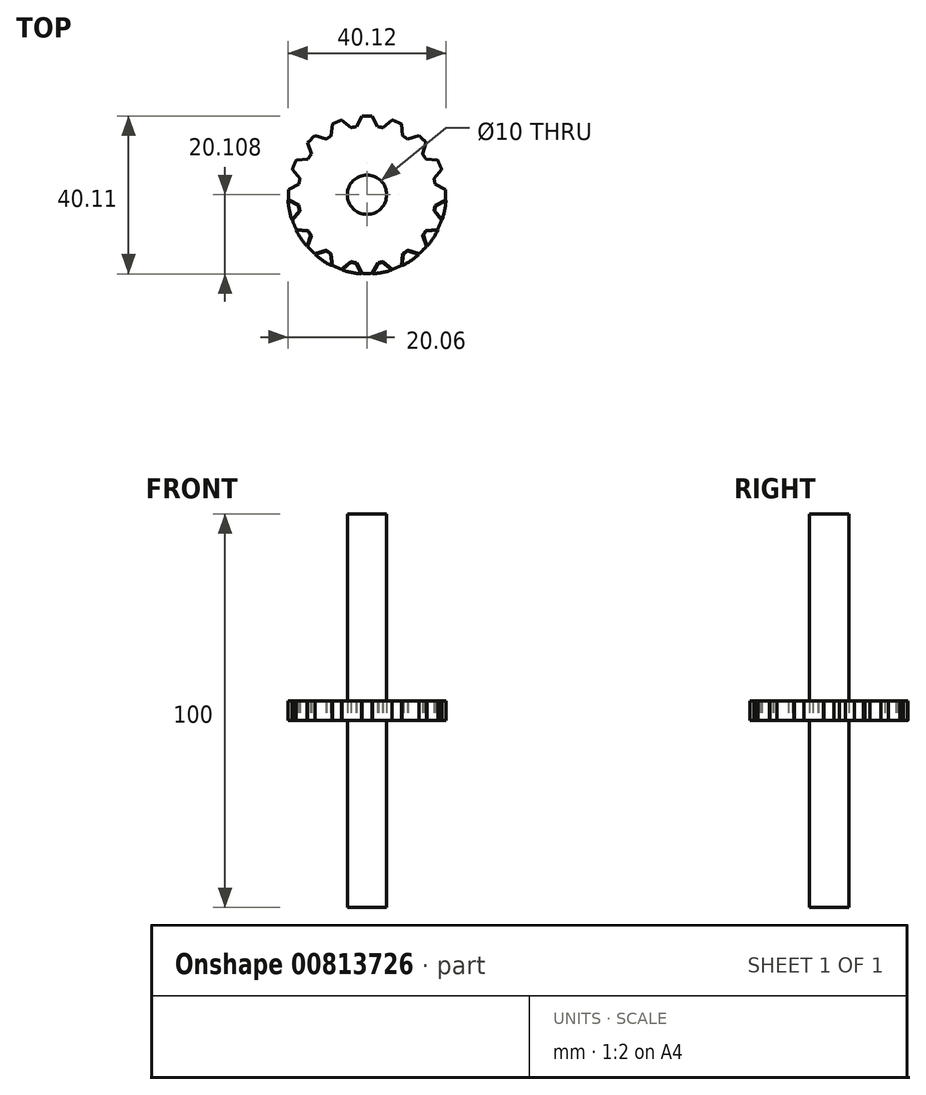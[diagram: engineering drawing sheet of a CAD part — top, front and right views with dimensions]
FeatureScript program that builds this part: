
annotation { "Feature Type Name" : "Feature", "Feature Type Description" : "" }
export const myFeature = defineFeature(function(context is Context, id is Id, definition is map)
    precondition{}
    {
        {
            var Q0;
            Q0=qCreatedBy(makeId("Top.planeOp"),FACE);
            var sketch = newSketch(context, id + "F0", { "sketchPlane" : qUnion([Q0])});
            skArc(sketch, "E0", {"start": v(-6.42, -74.24) * mm, "mid": v(-7.63, -74.7) * mm, "end": v(-8.8, -75.22) * mm});
            skCircle(sketch, "E1", {"center": v(0, -93.18) * mm, "radius": 5 * mm});
            skArc(sketch, "E2", {"start": v(-2.7, -75.9) * mm, "mid": v(-3.4, -76.02) * mm, "end": v(-4.1, -76.17) * mm});
            skLineSegment(sketch, "E3", {"start": v(-14.14, -82.87) * mm, "end": v(-15.04, -80) * mm});
            skLineSegment(sketch, "E4.MirrorCS", {"start": v(-10.3, -79.04) * mm, "end": v(-13.19, -78.15) * mm});
            skLineSegment(sketch, "E5.MirrorCS", {"start": v(-17.3, -90.49) * mm, "end": v(-19.96, -91.9) * mm});
            skLineSegment(sketch, "E6.MirrorCS", {"start": v(-2.7, -75.9) * mm, "end": v(-1.29, -73.22) * mm});
            skLineSegment(sketch, "E7.MirrorCS", {"start": v(-17.3, -95.88) * mm, "end": v(-19.96, -94.47) * mm});
            skLineSegment(sketch, "E8.MirrorCS", {"start": v(2.7, -75.9) * mm, "end": v(1.29, -73.22) * mm});
            skLineSegment(sketch, "E9.MirrorCS", {"start": v(10.3, -79.04) * mm, "end": v(13.19, -78.15) * mm});
            skLineSegment(sketch, "E10.MirrorCS", {"start": v(14.12, -82.85) * mm, "end": v(15, -79.96) * mm});
            skLineSegment(sketch, "E11.MirrorCS", {"start": v(17.3, -90.52) * mm, "end": v(19.96, -91.94) * mm});
            skLineSegment(sketch, "E12.MirrorCS", {"start": v(17.28, -95.94) * mm, "end": v(19.96, -94.5) * mm});
            skLineSegment(sketch, "E13.MirrorCS", {"start": v(14.16, -103.46) * mm, "end": v(15.06, -106.34) * mm});
            skLineSegment(sketch, "E14.MirrorCS", {"start": v(10.36, -107.29) * mm, "end": v(13.25, -108.16) * mm});
            skLineSegment(sketch, "E15.MirrorCS", {"start": v(-14.13, -103.5) * mm, "end": v(-15.04, -106.37) * mm});
            skLineSegment(sketch, "E16.MirrorCS", {"start": v(-10.34, -107.3) * mm, "end": v(-13.22, -108.2) * mm});
            skLineSegment(sketch, "E17.MirrorCS", {"start": v(2.8, -110.45) * mm, "end": v(1.33, -113.14) * mm});
            skLineSegment(sketch, "E18.MirrorCS", {"start": v(-2.67, -110.48) * mm, "end": v(-1.25, -113.14) * mm});
            skLineSegment(sketch, "E19.MirrorCS", {"start": v(14.96, -84.1) * mm, "end": v(17.96, -84.38) * mm});
            skLineSegment(sketch, "E20.MirrorCS", {"start": v(17.01, -89.08) * mm, "end": v(18.94, -86.76) * mm});
            skLineSegment(sketch, "E21.MirrorCS", {"start": v(17.02, -97.26) * mm, "end": v(18.94, -99.6) * mm});
            skLineSegment(sketch, "E22.MirrorCS", {"start": v(14.91, -102.34) * mm, "end": v(17.96, -101.98) * mm});
            skLineSegment(sketch, "E23.MirrorCS", {"start": v(9.08, -108.14) * mm, "end": v(8.8, -111.14) * mm});
            skLineSegment(sketch, "E24.MirrorCS", {"start": v(4.02, -110.21) * mm, "end": v(6.42, -112.12) * mm});
            skLineSegment(sketch, "E25.MirrorCS", {"start": v(-4.1, -110.2) * mm, "end": v(-6.42, -112.12) * mm});
            skLineSegment(sketch, "E26.MirrorCS", {"start": v(-9.1, -108.13) * mm, "end": v(-8.8, -111.14) * mm});
            skLineSegment(sketch, "E27.MirrorCS", {"start": v(-14.97, -102.25) * mm, "end": v(-17.96, -101.98) * mm});
            skLineSegment(sketch, "E28.MirrorCS", {"start": v(-17.01, -97.28) * mm, "end": v(-18.94, -99.6) * mm});
            skLineSegment(sketch, "E29.MirrorCS", {"start": v(-17.01, -89.08) * mm, "end": v(-18.94, -86.76) * mm});
            skLineSegment(sketch, "E30.MirrorCS", {"start": v(-14.96, -84.1) * mm, "end": v(-17.96, -84.38) * mm});
            skLineSegment(sketch, "E31.MirrorCS", {"start": v(-9.08, -78.22) * mm, "end": v(-8.8, -75.22) * mm});
            skLineSegment(sketch, "E32.MirrorCS", {"start": v(-4.1, -76.17) * mm, "end": v(-6.42, -74.24) * mm});
            skLineSegment(sketch, "E33.MirrorCS", {"start": v(4.1, -76.17) * mm, "end": v(6.42, -74.24) * mm});
            skLineSegment(sketch, "E34.MirrorCS", {"start": v(9.08, -78.22) * mm, "end": v(8.8, -75.22) * mm});
            skPoint(sketch, "E35.start.orphan", {"position": v(0, -88.18) * mm});
            skArc(sketch, "E36.trimOffspring", {"start": v(-9.08, -78.22) * mm, "mid": v(-9.7, -78.62) * mm, "end": v(-10.3, -79.04) * mm});
            skArc(sketch, "E37.trimOffspring", {"start": v(-14.14, -82.87) * mm, "mid": v(-14.56, -83.48) * mm, "end": v(-14.96, -84.1) * mm});
            skPoint(sketch, "E38.MirrorCS.end.orphan", {"position": v(-18.48, -85.54) * mm});
            skArc(sketch, "E39.trimOffspring", {"start": v(-17.01, -89.08) * mm, "mid": v(-17.17, -89.78) * mm, "end": v(-17.3, -90.49) * mm});
            skArc(sketch, "E40.trimOffspring", {"start": v(-17.3, -95.88) * mm, "mid": v(-17.17, -96.58) * mm, "end": v(-17.01, -97.28) * mm});
            skArc(sketch, "E41.trimOffspring", {"start": v(-19.96, -91.9) * mm, "mid": v(-20, -93.18) * mm, "end": v(-19.96, -94.47) * mm});
            skArc(sketch, "E42.trimOffspring", {"start": v(-17.96, -84.38) * mm, "mid": v(-18.49, -85.56) * mm, "end": v(-18.94, -86.76) * mm});
            skArc(sketch, "E43.trimOffspring", {"start": v(-13.19, -78.15) * mm, "mid": v(-14.14, -79.04) * mm, "end": v(-15.04, -80) * mm});
            skArc(sketch, "E44.trimOffspring", {"start": v(1.29, -73.22) * mm, "mid": v(0, -73.18) * mm, "end": v(-1.29, -73.22) * mm});
            skPoint(sketch, "E45.MirrorCS.end.orphan", {"position": v(7.64, -74.7) * mm});
            skArc(sketch, "E46.trimOffspring", {"start": v(4.1, -76.17) * mm, "mid": v(3.4, -76.02) * mm, "end": v(2.7, -75.9) * mm});
            skArc(sketch, "E47.trimOffspring", {"start": v(8.8, -75.22) * mm, "mid": v(7.63, -74.7) * mm, "end": v(6.42, -74.24) * mm});
            skArc(sketch, "E48.trimOffspring", {"start": v(10.3, -79.04) * mm, "mid": v(9.7, -78.62) * mm, "end": v(9.08, -78.22) * mm});
            skArc(sketch, "E49.trimOffspring", {"start": v(15, -79.96) * mm, "mid": v(14.13, -79.03) * mm, "end": v(13.19, -78.15) * mm});
            skPoint(sketch, "E50.orphan", {"position": v(18.48, -85.54) * mm});
            skArc(sketch, "E51.trimOffspring", {"start": v(14.96, -84.1) * mm, "mid": v(14.55, -83.46) * mm, "end": v(14.12, -82.85) * mm});
            skArc(sketch, "E52.trimOffspring", {"start": v(17.3, -90.52) * mm, "mid": v(17.17, -89.8) * mm, "end": v(17.01, -89.08) * mm});
            skArc(sketch, "E53.trimOffspring", {"start": v(17.02, -97.26) * mm, "mid": v(17.16, -96.6) * mm, "end": v(17.28, -95.94) * mm});
            skPoint(sketch, "E54.MirrorCS.end.orphan", {"position": v(18.48, -100.83) * mm});
            skArc(sketch, "E55.trimOffspring", {"start": v(14.16, -103.46) * mm, "mid": v(14.55, -102.9) * mm, "end": v(14.91, -102.34) * mm});
            skPoint(sketch, "E56.orphan", {"position": v(7.64, -111.66) * mm});
            skArc(sketch, "E57.trimOffspring", {"start": v(18.94, -86.76) * mm, "mid": v(18.49, -85.56) * mm, "end": v(17.96, -84.38) * mm});
            skArc(sketch, "E58.trimOffspring", {"start": v(19.96, -94.5) * mm, "mid": v(20, -93.22) * mm, "end": v(19.96, -91.94) * mm});
            skArc(sketch, "E59.trimOffspring", {"start": v(17.96, -101.98) * mm, "mid": v(18.49, -100.8) * mm, "end": v(18.94, -99.6) * mm});
            skArc(sketch, "E60.trimOffspring", {"start": v(13.25, -108.16) * mm, "mid": v(14.18, -107.28) * mm, "end": v(15.06, -106.34) * mm});
            skArc(sketch, "E61.trimOffspring", {"start": v(6.42, -112.12) * mm, "mid": v(7.63, -111.67) * mm, "end": v(8.8, -111.14) * mm});
            skArc(sketch, "E62.trimOffspring", {"start": v(-1.25, -113.14) * mm, "mid": v(0.04, -113.18) * mm, "end": v(1.33, -113.14) * mm});
            skArc(sketch, "E63.trimOffspring", {"start": v(-8.8, -111.14) * mm, "mid": v(-7.63, -111.67) * mm, "end": v(-6.42, -112.12) * mm});
            skArc(sketch, "E64.trimOffspring", {"start": v(-18.94, -99.6) * mm, "mid": v(-18.49, -100.8) * mm, "end": v(-17.96, -101.98) * mm});
            skArc(sketch, "E65.trimOffspring", {"start": v(-15.04, -106.37) * mm, "mid": v(-14.16, -107.3) * mm, "end": v(-13.22, -108.2) * mm});
            skArc(sketch, "E66.trimOffspring", {"start": v(-10.34, -107.3) * mm, "mid": v(-9.73, -107.73) * mm, "end": v(-9.1, -108.13) * mm});
            skArc(sketch, "E67.trimOffspring", {"start": v(-14.97, -102.25) * mm, "mid": v(-14.56, -102.89) * mm, "end": v(-14.13, -103.5) * mm});
            skPoint(sketch, "E68.orphan", {"position": v(-7.64, -111.66) * mm});
            skArc(sketch, "E69.trimOffspring", {"start": v(-4.1, -110.2) * mm, "mid": v(-3.4, -110.35) * mm, "end": v(-2.67, -110.48) * mm});
            skArc(sketch, "E70.trimOffspring", {"start": v(2.8, -110.45) * mm, "mid": v(3.42, -110.34) * mm, "end": v(4.02, -110.21) * mm});
            skArc(sketch, "E71.trimOffspring", {"start": v(9.08, -108.14) * mm, "mid": v(9.73, -107.73) * mm, "end": v(10.36, -107.29) * mm});
            skArc(sketch, "E72.2", {"start": v(-17.43, -95.97) * mm, "mid": v(-17.31, -96.61) * mm, "end": v(-17.18, -97.25) * mm});
            skLineSegment(sketch, "E72.3", {"start": v(-17.18, -97.25) * mm, "end": v(-18.88, -99.3) * mm});
            skLineSegment(sketch, "E73.1", {"start": v(-15.06, -102.4) * mm, "end": v(-17.7, -102.15) * mm});
            skArc(sketch, "E73.2", {"start": v(-15.06, -102.4) * mm, "mid": v(-14.69, -102.97) * mm, "end": v(-14.3, -103.53) * mm});
            skLineSegment(sketch, "E73.3", {"start": v(-14.3, -103.53) * mm, "end": v(-15.1, -106.07) * mm});
            skLineSegment(sketch, "E74.0", {"start": v(-10.36, -107.47) * mm, "end": v(-12.92, -108.25) * mm});
            skArc(sketch, "E74.1", {"start": v(-10.36, -107.47) * mm, "mid": v(-9.81, -107.85) * mm, "end": v(-9.25, -108.22) * mm});
            skLineSegment(sketch, "E74.2", {"start": v(-9.25, -108.22) * mm, "end": v(-8.98, -110.89) * mm});
            skLineSegment(sketch, "E75.0", {"start": v(-4.06, -110.36) * mm, "end": v(-6.12, -112.07) * mm});
            skArc(sketch, "E75.1", {"start": v(-4.06, -110.36) * mm, "mid": v(-3.42, -110.5) * mm, "end": v(-2.77, -110.61) * mm});
            skLineSegment(sketch, "E75.2", {"start": v(-2.77, -110.61) * mm, "end": v(-1.5, -112.97) * mm});
            skLineSegment(sketch, "E76.1", {"start": v(2.9, -110.6) * mm, "end": v(1.6, -112.97) * mm});
            skArc(sketch, "E76.2", {"start": v(2.9, -110.6) * mm, "mid": v(3.45, -110.5) * mm, "end": v(3.99, -110.38) * mm});
            skLineSegment(sketch, "E76.3", {"start": v(3.99, -110.38) * mm, "end": v(6.11, -112.07) * mm});
            skLineSegment(sketch, "E77.0", {"start": v(9.23, -108.23) * mm, "end": v(8.97, -110.89) * mm});
            skArc(sketch, "E77.1", {"start": v(9.23, -108.23) * mm, "mid": v(9.81, -107.85) * mm, "end": v(10.38, -107.45) * mm});
            skLineSegment(sketch, "E77.2", {"start": v(10.38, -107.45) * mm, "end": v(12.95, -108.23) * mm});
            skLineSegment(sketch, "E78.0", {"start": v(14.33, -103.49) * mm, "end": v(15.12, -106.04) * mm});
            skArc(sketch, "E78.1", {"start": v(14.33, -103.49) * mm, "mid": v(14.67, -102.99) * mm, "end": v(15, -102.48) * mm});
            skLineSegment(sketch, "E78.2", {"start": v(15, -102.48) * mm, "end": v(17.7, -102.16) * mm});
            skLineSegment(sketch, "E79.1", {"start": v(17.18, -97.22) * mm, "end": v(18.88, -99.3) * mm});
            skArc(sketch, "E79.2", {"start": v(17.18, -97.22) * mm, "mid": v(17.3, -96.63) * mm, "end": v(17.42, -96.03) * mm});
            skLineSegment(sketch, "E79.3", {"start": v(17.42, -96.03) * mm, "end": v(19.79, -94.77) * mm});
            skPoint(sketch, "E80.startSnap0", {"position": v(20, -93.22) * mm});
            skLineSegment(sketch, "E81", {"start": v(-19.96, -91.9) * mm, "end": v(-19.96, -94.47) * mm});
            skLineSegment(sketch, "E82", {"start": v(-19.96, -93.18) * mm, "end": v(-20.1, -93.18) * mm});
            skLineSegment(sketch, "E83", {"start": v(19.96, -91.94) * mm, "end": v(19.96, -94.5) * mm});
            skLineSegment(sketch, "E84", {"start": v(19.96, -93.22) * mm, "end": v(20.1, -93.22) * mm});
            skArc(sketch, "E85.MirrorCS", {"start": v(19.96, 15.8) * mm, "mid": v(20, 14.5) * mm, "end": v(19.96, 13.22) * mm});
            skLineSegment(sketch, "E86.MirrorCS", {"start": v(17.42, 17.32) * mm, "end": v(19.79, 16.06) * mm});
            skArc(sketch, "E87.MirrorCS", {"start": v(-4.1, 31.48) * mm, "mid": v(-3.4, 31.64) * mm, "end": v(-2.67, 31.76) * mm});
            skArc(sketch, "E88.MirrorCS", {"start": v(9.23, 29.52) * mm, "mid": v(9.81, 29.14) * mm, "end": v(10.38, 28.74) * mm});
            skLineSegment(sketch, "E89.MirrorCS", {"start": v(-10.34, 28.59) * mm, "end": v(-13.22, 29.48) * mm});
            skLineSegment(sketch, "E90.MirrorCS", {"start": v(15, 23.77) * mm, "end": v(17.7, 23.45) * mm});
            skArc(sketch, "E91.MirrorCS", {"start": v(18.94, 20.89) * mm, "mid": v(19.61, 18.37) * mm, "end": v(19.96, 15.8) * mm});
            skLineSegment(sketch, "E92.MirrorCS", {"start": v(-9.25, 29.5) * mm, "end": v(-8.98, 32.17) * mm});
            skLineSegment(sketch, "E93.MirrorCS", {"start": v(19.96, 13.22) * mm, "end": v(19.96, 15.8) * mm});
            skLineSegment(sketch, "E94.MirrorCS", {"start": v(10.38, 28.74) * mm, "end": v(12.95, 29.52) * mm});
            skArc(sketch, "E95.MirrorCS", {"start": v(-17.43, 17.26) * mm, "mid": v(-17.31, 17.9) * mm, "end": v(-17.18, 18.53) * mm});
            skLineSegment(sketch, "E96.MirrorCS", {"start": v(17.02, 18.55) * mm, "end": v(18.94, 20.89) * mm});
            skArc(sketch, "E97.MirrorCS", {"start": v(-10.36, 28.76) * mm, "mid": v(-9.81, 29.14) * mm, "end": v(-9.25, 29.5) * mm});
            skLineSegment(sketch, "E98.MirrorCS", {"start": v(-4.06, 31.64) * mm, "end": v(-6.12, 33.35) * mm});
            skLineSegment(sketch, "E99.MirrorCS", {"start": v(-2.67, 31.76) * mm, "end": v(-1.25, 34.43) * mm});
            skArc(sketch, "E100.MirrorCS", {"start": v(2.8, 31.74) * mm, "mid": v(3.42, 31.63) * mm, "end": v(4.02, 31.5) * mm});
            skLineSegment(sketch, "E101.MirrorCS", {"start": v(14.33, 24.77) * mm, "end": v(15.12, 27.32) * mm});
            skLineSegment(sketch, "E102.MirrorCS", {"start": v(4.02, 31.5) * mm, "end": v(6.42, 33.4) * mm});
            skLineSegment(sketch, "E103.MirrorCS", {"start": v(17.28, 17.22) * mm, "end": v(19.96, 15.8) * mm});
            skArc(sketch, "E104.MirrorCS", {"start": v(-19.96, 13.18) * mm, "mid": v(-20, 14.47) * mm, "end": v(-19.96, 15.75) * mm});
            skArc(sketch, "E105.MirrorCS", {"start": v(14.33, 24.77) * mm, "mid": v(14.67, 24.28) * mm, "end": v(15, 23.77) * mm});
            skLineSegment(sketch, "E106.MirrorCS", {"start": v(2.8, 31.74) * mm, "end": v(1.33, 34.42) * mm});
            skLineSegment(sketch, "E107.MirrorCS", {"start": v(19.96, 14.5) * mm, "end": v(20.1, 14.5) * mm});
            skArc(sketch, "E108.MirrorCS", {"start": v(17.18, 18.5) * mm, "mid": v(17.3, 17.92) * mm, "end": v(17.42, 17.32) * mm});
            skArc(sketch, "E109.MirrorCS", {"start": v(15.06, 27.63) * mm, "mid": v(16.65, 25.54) * mm, "end": v(17.96, 23.27) * mm});
            skArc(sketch, "E110.MirrorCS", {"start": v(14.16, 24.75) * mm, "mid": v(14.55, 24.2) * mm, "end": v(14.91, 23.63) * mm});
            skLineSegment(sketch, "E111.MirrorCS", {"start": v(10.36, 28.57) * mm, "end": v(13.25, 29.45) * mm});
            skArc(sketch, "E112.MirrorCS", {"start": v(-10.34, 28.59) * mm, "mid": v(-9.73, 29.01) * mm, "end": v(-9.1, 29.41) * mm});
            skLineSegment(sketch, "E113.MirrorCS", {"start": v(-14.3, 24.82) * mm, "end": v(-15.1, 27.36) * mm});
            skLineSegment(sketch, "E114.MirrorCS", {"start": v(-10.36, 28.76) * mm, "end": v(-12.92, 29.54) * mm});
            skArc(sketch, "E115.MirrorCS", {"start": v(-6.42, 33.4) * mm, "mid": v(-3.87, 34.1) * mm, "end": v(-1.25, 34.43) * mm});
            skArc(sketch, "E116.MirrorCS", {"start": v(17.96, 23.27) * mm, "mid": v(18.49, 22.1) * mm, "end": v(18.94, 20.89) * mm});
            skLineSegment(sketch, "E117.MirrorCS", {"start": v(-14.13, 24.8) * mm, "end": v(-15.04, 27.66) * mm});
            skArc(sketch, "E118.MirrorCS", {"start": v(-4.06, 31.64) * mm, "mid": v(-3.42, 31.78) * mm, "end": v(-2.77, 31.9) * mm});
            skLineSegment(sketch, "E119.MirrorCS", {"start": v(9.23, 29.52) * mm, "end": v(8.97, 32.17) * mm});
            skLineSegment(sketch, "E120.MirrorCS", {"start": v(-19.96, 14.47) * mm, "end": v(-20.1, 14.47) * mm});
            skLineSegment(sketch, "E121.MirrorCS", {"start": v(2.9, 31.88) * mm, "end": v(1.6, 34.25) * mm});
            skLineSegment(sketch, "E122.MirrorCS", {"start": v(-17.43, 17.26) * mm, "end": v(-19.79, 16.01) * mm});
            skArc(sketch, "E123.MirrorCS", {"start": v(-13.22, 29.48) * mm, "mid": v(-11.1, 31.1) * mm, "end": v(-8.8, 32.43) * mm});
            skLineSegment(sketch, "E124.MirrorCS", {"start": v(-2.77, 31.9) * mm, "end": v(-1.5, 34.26) * mm});
            skArc(sketch, "E125.MirrorCS", {"start": v(1.33, 34.42) * mm, "mid": v(3.9, 34.08) * mm, "end": v(6.42, 33.4) * mm});
            skArc(sketch, "E126.MirrorCS", {"start": v(-1.25, 34.43) * mm, "mid": v(0.04, 34.47) * mm, "end": v(1.33, 34.42) * mm});
            skLineSegment(sketch, "E127.MirrorCS", {"start": v(-19.96, 13.18) * mm, "end": v(-19.96, 15.75) * mm});
            skArc(sketch, "E128.MirrorCS", {"start": v(2.9, 31.88) * mm, "mid": v(3.45, 31.78) * mm, "end": v(3.99, 31.66) * mm});
            skArc(sketch, "E129.MirrorCS", {"start": v(-15.04, 27.66) * mm, "mid": v(-14.16, 28.6) * mm, "end": v(-13.22, 29.48) * mm});
            skLineSegment(sketch, "E130.MirrorCS", {"start": v(-15.06, 23.68) * mm, "end": v(-17.7, 23.44) * mm});
            skArc(sketch, "E131.MirrorCS", {"start": v(13.25, 29.45) * mm, "mid": v(14.18, 28.57) * mm, "end": v(15.06, 27.63) * mm});
            skArc(sketch, "E132.MirrorCS", {"start": v(-15.06, 23.68) * mm, "mid": v(-14.69, 24.26) * mm, "end": v(-14.3, 24.82) * mm});
            skArc(sketch, "E133.MirrorCS", {"start": v(8.8, 32.43) * mm, "mid": v(11.12, 31.09) * mm, "end": v(13.25, 29.45) * mm});
            skArc(sketch, "E134.MirrorCS", {"start": v(-19.96, 15.75) * mm, "mid": v(-19.62, 18.36) * mm, "end": v(-18.94, 20.89) * mm});
            skArc(sketch, "E135.MirrorCS", {"start": v(17.02, 18.55) * mm, "mid": v(17.16, 17.89) * mm, "end": v(17.28, 17.22) * mm});
            skArc(sketch, "E136.MirrorCS", {"start": v(9.08, 29.43) * mm, "mid": v(9.73, 29.01) * mm, "end": v(10.36, 28.57) * mm});
            skLineSegment(sketch, "E137.MirrorCS", {"start": v(-4.1, 31.48) * mm, "end": v(-6.42, 33.4) * mm});
            skLineSegment(sketch, "E138.MirrorCS", {"start": v(9.08, 29.43) * mm, "end": v(8.8, 32.43) * mm});
            skLineSegment(sketch, "E139.MirrorCS", {"start": v(-17.18, 18.53) * mm, "end": v(-18.88, 20.59) * mm});
            skLineSegment(sketch, "E140.MirrorCS", {"start": v(3.99, 31.66) * mm, "end": v(6.11, 33.35) * mm});
            skArc(sketch, "E141.MirrorCS", {"start": v(6.42, 33.4) * mm, "mid": v(7.63, 32.96) * mm, "end": v(8.8, 32.43) * mm});
            skLineSegment(sketch, "E142.MirrorCS", {"start": v(17.18, 18.5) * mm, "end": v(18.88, 20.58) * mm});
            skLineSegment(sketch, "E143.MirrorCS", {"start": v(14.91, 23.63) * mm, "end": v(17.96, 23.27) * mm});
            skLineSegment(sketch, "E144.MirrorCS", {"start": v(-17.3, 17.16) * mm, "end": v(-19.96, 15.75) * mm});
            skLineSegment(sketch, "E145.MirrorCS", {"start": v(-9.1, 29.41) * mm, "end": v(-8.8, 32.43) * mm});
            skLineSegment(sketch, "E146.MirrorCS", {"start": v(14.16, 24.75) * mm, "end": v(15.06, 27.63) * mm});
            skArc(sketch, "E147.MirrorCS", {"start": v(-8.8, 32.43) * mm, "mid": v(-7.63, 32.96) * mm, "end": v(-6.42, 33.4) * mm});
            skArc(sketch, "E148.MirrorCS", {"start": v(-17.96, 23.27) * mm, "mid": v(-16.64, 25.56) * mm, "end": v(-15.04, 27.66) * mm});
            skArc(sketch, "E149.MirrorCS", {"start": v(-14.97, 23.53) * mm, "mid": v(-14.56, 24.17) * mm, "end": v(-14.13, 24.8) * mm});
            skLineSegment(sketch, "E150.MirrorCS", {"start": v(-17.01, 18.57) * mm, "end": v(-18.94, 20.89) * mm});
            skArc(sketch, "E151.MirrorCS", {"start": v(-18.94, 20.89) * mm, "mid": v(-18.49, 22.1) * mm, "end": v(-17.96, 23.27) * mm});
            skArc(sketch, "E152.MirrorCS", {"start": v(-17.3, 17.16) * mm, "mid": v(-17.17, 17.87) * mm, "end": v(-17.01, 18.57) * mm});
            skLineSegment(sketch, "E153.MirrorCS", {"start": v(-14.97, 23.53) * mm, "end": v(-17.96, 23.27) * mm});
            skArc(sketch, "E154.MirrorCS", {"start": v(17.3, 11.8) * mm, "mid": v(17.17, 11.08) * mm, "end": v(17.01, 10.37) * mm});
            skLineSegment(sketch, "E155.MirrorCS", {"start": v(-17.3, 11.77) * mm, "end": v(-19.96, 13.18) * mm});
            skLineSegment(sketch, "E156.MirrorCS", {"start": v(17.3, 11.8) * mm, "end": v(19.96, 13.22) * mm});
            skArc(sketch, "E157.MirrorCS", {"start": v(10.3, 0.33) * mm, "mid": v(9.7, -0.1) * mm, "end": v(9.08, -0.49) * mm});
            skLineSegment(sketch, "E158.MirrorCS", {"start": v(17.01, 10.37) * mm, "end": v(18.94, 8.05) * mm});
            skLineSegment(sketch, "E159.MirrorCS", {"start": v(-14.96, 5.38) * mm, "end": v(-17.96, 5.67) * mm});
            skLineSegment(sketch, "E160.MirrorCS", {"start": v(-4.1, -2.54) * mm, "end": v(-6.42, -4.47) * mm});
            skLineSegment(sketch, "E161.MirrorCS", {"start": v(-10.3, 0.33) * mm, "end": v(-13.19, -0.57) * mm});
            skLineSegment(sketch, "E162.MirrorCS", {"start": v(-17.01, 10.37) * mm, "end": v(-18.94, 8.05) * mm});
            skLineSegment(sketch, "E163.MirrorCS", {"start": v(14.96, 5.38) * mm, "end": v(17.96, 5.67) * mm});
            skLineSegment(sketch, "E164.MirrorCS", {"start": v(4.1, -2.54) * mm, "end": v(6.42, -4.47) * mm});
            skLineSegment(sketch, "E165.MirrorCS", {"start": v(9.08, -0.49) * mm, "end": v(8.8, -3.5) * mm});
            skArc(sketch, "E166.MirrorCS", {"start": v(18.94, 8.05) * mm, "mid": v(18.49, 6.84) * mm, "end": v(17.96, 5.67) * mm});
            skLineSegment(sketch, "E167.MirrorCS", {"start": v(2.7, -2.82) * mm, "end": v(1.29, -5.5) * mm});
            skLineSegment(sketch, "E168.MirrorCS", {"start": v(-14.14, 4.16) * mm, "end": v(-15.04, 1.28) * mm});
            skLineSegment(sketch, "E169.MirrorCS", {"start": v(-2.7, -2.82) * mm, "end": v(-1.29, -5.5) * mm});
            skLineSegment(sketch, "E170.MirrorCS", {"start": v(14.12, 4.13) * mm, "end": v(15, 1.25) * mm});
            skArc(sketch, "E171.MirrorCS", {"start": v(-6.42, -4.47) * mm, "mid": v(-7.63, -4.02) * mm, "end": v(-8.8, -3.5) * mm});
            skArc(sketch, "E172.MirrorCS", {"start": v(-17.96, 5.67) * mm, "mid": v(-18.49, 6.84) * mm, "end": v(-18.94, 8.05) * mm});
            skArc(sketch, "E173.MirrorCS", {"start": v(8.8, -3.5) * mm, "mid": v(7.63, -4.02) * mm, "end": v(6.42, -4.47) * mm});
            skArc(sketch, "E174.MirrorCS", {"start": v(-2.7, -2.82) * mm, "mid": v(-3.4, -2.7) * mm, "end": v(-4.1, -2.54) * mm});
            skArc(sketch, "E175.MirrorCS", {"start": v(-9.08, -0.49) * mm, "mid": v(-9.7, -0.1) * mm, "end": v(-10.3, 0.33) * mm});
            skArc(sketch, "E176.MirrorCS", {"start": v(15, 1.25) * mm, "mid": v(14.13, 0.31) * mm, "end": v(13.19, -0.57) * mm});
            skArc(sketch, "E177.MirrorCS", {"start": v(1.29, -5.5) * mm, "mid": v(0, -5.53) * mm, "end": v(-1.29, -5.5) * mm});
            skArc(sketch, "E178.MirrorCS", {"start": v(4.1, -2.54) * mm, "mid": v(3.4, -2.7) * mm, "end": v(2.7, -2.82) * mm});
            skArc(sketch, "E179.MirrorCS", {"start": v(14.96, 5.38) * mm, "mid": v(14.55, 4.75) * mm, "end": v(14.12, 4.13) * mm});
            skArc(sketch, "E180.MirrorCS", {"start": v(-17.01, 10.37) * mm, "mid": v(-17.17, 11.07) * mm, "end": v(-17.3, 11.77) * mm});
            skArc(sketch, "E181.MirrorCS", {"start": v(-14.14, 4.16) * mm, "mid": v(-14.56, 4.76) * mm, "end": v(-14.96, 5.38) * mm});
            skLineSegment(sketch, "E182.MirrorCS", {"start": v(-9.08, -0.49) * mm, "end": v(-8.8, -3.5) * mm});
            skArc(sketch, "E183.MirrorCS", {"start": v(-13.19, -0.57) * mm, "mid": v(-14.14, 0.33) * mm, "end": v(-15.04, 1.28) * mm});
            skLineSegment(sketch, "E184.MirrorCS", {"start": v(10.3, 0.33) * mm, "end": v(13.19, -0.57) * mm});
            skPoint(sketch, "E185.MirrorP", {"position": v(-7.64, 32.95) * mm});
            skPoint(sketch, "E186.MirrorP", {"position": v(18.48, 22.11) * mm});
            skPoint(sketch, "E187.MirrorP", {"position": v(7.64, 32.95) * mm});
            skPoint(sketch, "E188.MirrorP", {"position": v(0, 9.47) * mm});
            skPoint(sketch, "E189.MirrorP", {"position": v(18.48, 6.82) * mm});
            skPoint(sketch, "E190.MirrorP", {"position": v(20, 14.5) * mm});
            skPoint(sketch, "E191.MirrorP", {"position": v(-18.48, 6.82) * mm});
            skCircle(sketch, "E192.MirrorC", {"center": v(0, 14.47) * mm, "radius": 5 * mm});
            skPoint(sketch, "E193.MirrorP", {"position": v(7.64, -4.01) * mm});
            skLineSegment(sketch, "E194", {"start": v(-20.1, -93.18) * mm, "end": v(-20.1, 14.47) * mm});
            skLineSegment(sketch, "E195", {"start": v(20.1, 14.5) * mm, "end": v(20.1, -93.22) * mm});
            skArc(sketch, "E196", {"start": v(-20.1, -93.18) * mm, "mid": v(-0.02, -113.33) * mm, "end": v(20.1, -93.22) * mm});
            skLineSegment(sketch, "E197", {"start": v(-17.43, -95.97) * mm, "end": v(-20.06, -94.58) * mm});
            skLineSegment(sketch, "E198", {"start": v(-17.18, -97.25) * mm, "end": v(-19.09, -99.54) * mm});
            skLineSegment(sketch, "E199", {"start": v(17.42, -96.03) * mm, "end": v(20.06, -94.62) * mm});
            skLineSegment(sketch, "E200", {"start": v(17.18, -97.22) * mm, "end": v(19.09, -99.55) * mm});
            skLineSegment(sketch, "E201", {"start": v(15, -102.48) * mm, "end": v(18.03, -102.12) * mm});
            skLineSegment(sketch, "E202", {"start": v(10.38, -107.45) * mm, "end": v(13.27, -108.33) * mm});
            skLineSegment(sketch, "E203", {"start": v(9.23, -108.23) * mm, "end": v(8.94, -111.23) * mm});
            skLineSegment(sketch, "E204", {"start": v(3.99, -110.38) * mm, "end": v(6.39, -112.29) * mm});
            skLineSegment(sketch, "E205", {"start": v(2.9, -110.6) * mm, "end": v(1.42, -113.28) * mm});
            skLineSegment(sketch, "E206", {"start": v(14.33, -103.49) * mm, "end": v(15.23, -106.36) * mm});
            skLineSegment(sketch, "E207", {"start": v(-2.77, -110.61) * mm, "end": v(-1.34, -113.29) * mm});
            skLineSegment(sketch, "E208", {"start": v(-4.06, -110.36) * mm, "end": v(-6.39, -112.29) * mm});
            skLineSegment(sketch, "E209", {"start": v(-9.25, -108.22) * mm, "end": v(-8.94, -111.23) * mm});
            skLineSegment(sketch, "E210", {"start": v(-10.36, -107.47) * mm, "end": v(-13.24, -108.36) * mm});
            skLineSegment(sketch, "E211", {"start": v(-15.06, -102.4) * mm, "end": v(-18.03, -102.13) * mm});
            skLineSegment(sketch, "E212", {"start": v(-14.3, -103.53) * mm, "end": v(-15.2, -106.39) * mm});
            skLineSegment(sketch, "E213", {"start": v(0, -73.18) * mm, "end": v(0, -5.5) * mm});
            skLineSegment(sketch, "E214", {"start": v(0, -39.34) * mm, "end": v(13.05, -39.34) * mm});
            skSolve(sketch);
        }
        {
            var Q0;
            Q0=makeQuery(id+"F0.imprint","IMPRINT",FACE,{"disambiguationData":[TD([[makeQuery(id+"F0.imprint","IMPRINT",EDGE,{"derivedFrom":sQuery(id+"F0.wireOp",EDGE,"a3mfgiQM-TKiU-O9W0-hxFl-bYzTbnojI0ci")}),1.0]])]});
            var Q1;
            Q1=makeQuery(id+"F0.imprint","IMPRINT",FACE,{"disambiguationData":[TD([[makeQuery(id+"F0.imprint","IMPRINT",EDGE,{"derivedFrom":sQuery(id+"F0.wireOp",EDGE,"E1")}),1.0]])]});
            var Q2;
            Q2=makeQuery(id+"F0.imprint","IMPRINT",FACE,{"disambiguationData":[TD([[makeQuery(id+"F0.imprint","IMPRINT",EDGE,{"derivedFrom":sQuery(id+"F0.wireOp",EDGE,"be3ca94d-eb1c-49fd-af19-4feb1019829573.MirrorC")}),-1.0]])]});
            extrude(context, id + "F1", {"entities" : qUnion([Q0, Q1, Q2]), "endBound" : BoundingType.SYMMETRIC, "depth" : 100 * mm, "offsetDistance" : 25 * mm});
        }
        {
            var Q0;
            Q0=makeQuery(id+"F0.imprint","IMPRINT",FACE,{"disambiguationData":[TD([[makeQuery(id+"F0.imprint","IMPRINT",EDGE,{"derivedFrom":sQuery(id+"F0.wireOp",EDGE,"E0")}),1.0]])]});
            var Q1;
            Q1=makeQuery(id+"F0.imprint","IMPRINT",FACE,{"disambiguationData":[TD([[makeQuery(id+"F0.imprint","IMPRINT",EDGE,{"derivedFrom":sQuery(id+"F0.wireOp",EDGE,"be3ca94d-eb1c-49fd-af19-4feb101982956.MirrorCS")}),-1.0]])]});
            extrude(context, id + "F2", {"entities" : qUnion([Q0, Q1]), "endBound" : BoundingType.SYMMETRIC, "depth" : 5 * mm, "offsetDistance" : 25 * mm});
        }
        {
            var Q0;
            {var subQ1=sQuery(id+"F0.wireOp",EDGE,"E72.2");Q0=makeQuery(id+"F0.imprint","IMPRINT",FACE,{"disambiguationData":[TD([[makeQuery(id+"F0.imprint","IMPRINT",EDGE,{"derivedFrom":subQ1}),-1.0]])]});}
            var Q1;
            {var subQ4=sQuery(id+"F0.wireOp",EDGE,"E79.2");Q1=makeQuery(id+"F0.imprint","IMPRINT",FACE,{"disambiguationData":[TD([[makeQuery(id+"F0.imprint","IMPRINT",EDGE,{"derivedFrom":subQ4}),-1.0]])]});}
            var Q2;
            {var subQ4=sQuery(id+"F0.wireOp",EDGE,"E77.1");Q2=makeQuery(id+"F0.imprint","IMPRINT",FACE,{"disambiguationData":[TD([[makeQuery(id+"F0.imprint","IMPRINT",EDGE,{"derivedFrom":subQ4}),-1.0]])]});}
            var Q3;
            {var subQ4=sQuery(id+"F0.wireOp",EDGE,"E76.2");Q3=makeQuery(id+"F0.imprint","IMPRINT",FACE,{"disambiguationData":[TD([[makeQuery(id+"F0.imprint","IMPRINT",EDGE,{"derivedFrom":subQ4}),-1.0]])]});}
            var Q4;
            {var subQ4=sQuery(id+"F0.wireOp",EDGE,"E78.1");Q4=makeQuery(id+"F0.imprint","IMPRINT",FACE,{"disambiguationData":[TD([[makeQuery(id+"F0.imprint","IMPRINT",EDGE,{"derivedFrom":subQ4}),-1.0]])]});}
            var Q5;
            {var subQ1=sQuery(id+"F0.wireOp",EDGE,"E75.1");Q5=makeQuery(id+"F0.imprint","IMPRINT",FACE,{"disambiguationData":[TD([[makeQuery(id+"F0.imprint","IMPRINT",EDGE,{"derivedFrom":subQ1}),-1.0]])]});}
            var Q6;
            {var subQ4=sQuery(id+"F0.wireOp",EDGE,"E74.1");Q6=makeQuery(id+"F0.imprint","IMPRINT",FACE,{"disambiguationData":[TD([[makeQuery(id+"F0.imprint","IMPRINT",EDGE,{"derivedFrom":subQ4}),-1.0]])]});}
            var Q7;
            {var subQ1=sQuery(id+"F0.wireOp",EDGE,"E73.2");Q7=makeQuery(id+"F0.imprint","IMPRINT",FACE,{"disambiguationData":[TD([[makeQuery(id+"F0.imprint","IMPRINT",EDGE,{"derivedFrom":subQ1}),-1.0]])]});}
            extrude(context, id + "F3", {"entities" : qUnion([Q0, Q1, Q2, Q3, Q4, Q5, Q6, Q7]), "endBound" : BoundingType.SYMMETRIC, "depth" : 5 * mm, "offsetDistance" : 25 * mm});
        }
        {
            var Q0;
            Q0=sQuery(id+"F0.wireOp",EDGE,"E196");
            extrude(context, id + "F4", {"bodyType" : ToolBodyType.SURFACE, "surfaceEntities" : qUnion([Q0]), "endBound" : BoundingType.SYMMETRIC, "depth" : 5 * mm, "offsetDistance" : 25 * mm});
        }
    });
